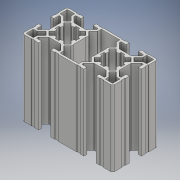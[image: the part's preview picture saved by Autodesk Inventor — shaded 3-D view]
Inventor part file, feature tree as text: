
AUTODESK INVENTOR PART (.ipt)
format: ipt  version: 2018 (Build 220112000, 112)  size: 575,488 bytes
history: native  units: mm
features: other x1, extrude x1, sketch x1
ambient origin geometry x8: Origin, YZ Plane, XZ Plane, XY Plane, X Axis, Y Axis, Z Axis, Center Point
bodies: Body1 (feature_tree)
feature tree (3):
  other  "Sólido1"
  extrude  "Extrusão1"  [1 undecoded]
  sketch  "Esboço1"  dims[d0=50.0mm d1=0.0mm]
note: 1 required parameter value undecoded (feature->parameter linkage not recoverable at this tier; creation-order binding heuristic only, values carry confidence <= 0.55)
